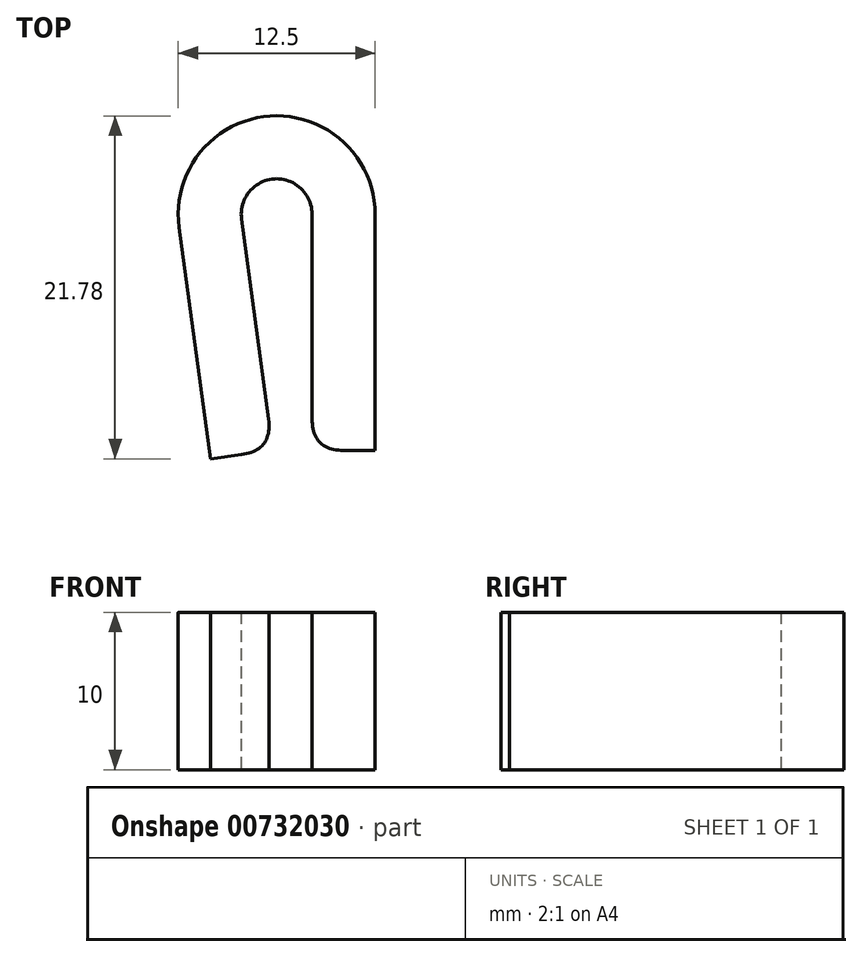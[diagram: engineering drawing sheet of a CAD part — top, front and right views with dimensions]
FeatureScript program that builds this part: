
annotation { "Feature Type Name" : "Feature", "Feature Type Description" : "" }
export const myFeature = defineFeature(function(context is Context, id is Id, definition is map)
    precondition{}
    {
        {
            var Q0;
            Q0=qCreatedBy(makeId("Top.planeOp"),FACE);
            var sketch = newSketch(context, id + "F0", { "sketchPlane" : qUnion([Q0])});
            skArc(sketch, "E0", {"start": v(2.25, 0) * mm, "mid": v(-0.15, 2.24) * mm, "end": v(-2.23, -0.3) * mm});
            skLineSegment(sketch, "E1", {"start": v(2.25, 0) * mm, "end": v(2.25, -15) * mm});
            skLineSegment(sketch, "E2", {"start": v(-2.23, -0.3) * mm, "end": v(-0.25, -15) * mm});
            skLineSegment(sketch, "E3.0", {"start": v(6.25, 0) * mm, "end": v(6.25, -15) * mm});
            skArc(sketch, "E3.1", {"start": v(6.25, 0) * mm, "mid": v(-0.42, 6.24) * mm, "end": v(-6.2, -0.83) * mm});
            skLineSegment(sketch, "E3.2", {"start": v(-6.2, -0.83) * mm, "end": v(-4.21, -15.53) * mm});
            skLineSegment(sketch, "E4", {"start": v(6.25, -15) * mm, "end": v(2.25, -15) * mm});
            skLineSegment(sketch, "E5", {"start": v(-0.25, -15) * mm, "end": v(-4.21, -15.53) * mm});
            skSolve(sketch);
        }
        {
            var Q0;
            Q0 = qSketchRegion(id + "F0", true);
            extrude(context, id + "F1", {"entities" : qUnion([Q0]), "depth" : 10 * mm, "offsetDistance" : 25 * mm});
        }
        {
            var Q0;
            Q0=makeQuery(id+"F1.opExtrude","SWEPT_EDGE",EDGE,{"disambiguationData":[OSD([sQuery(id+"F0.wireOp",EDGE,"E2"),sQuery(id+"F0.wireOp",EDGE,"E5")])]});
            var Q1;
            Q1=makeQuery(id+"F1.opExtrude","SWEPT_EDGE",EDGE,{"disambiguationData":[OSD([sQuery(id+"F0.wireOp",EDGE,"E1"),sQuery(id+"F0.wireOp",EDGE,"E4")])]});
            fillet(context, id + "F2", {"entities" : qUnion([Q0, Q1]), "radius" : 2 * mm, "tangentPropagation" : true, "rho" : 0.5, "crossSection" : FilletCrossSection.CONIC, "allowEdgeOverflow" : false});
        }
    });
